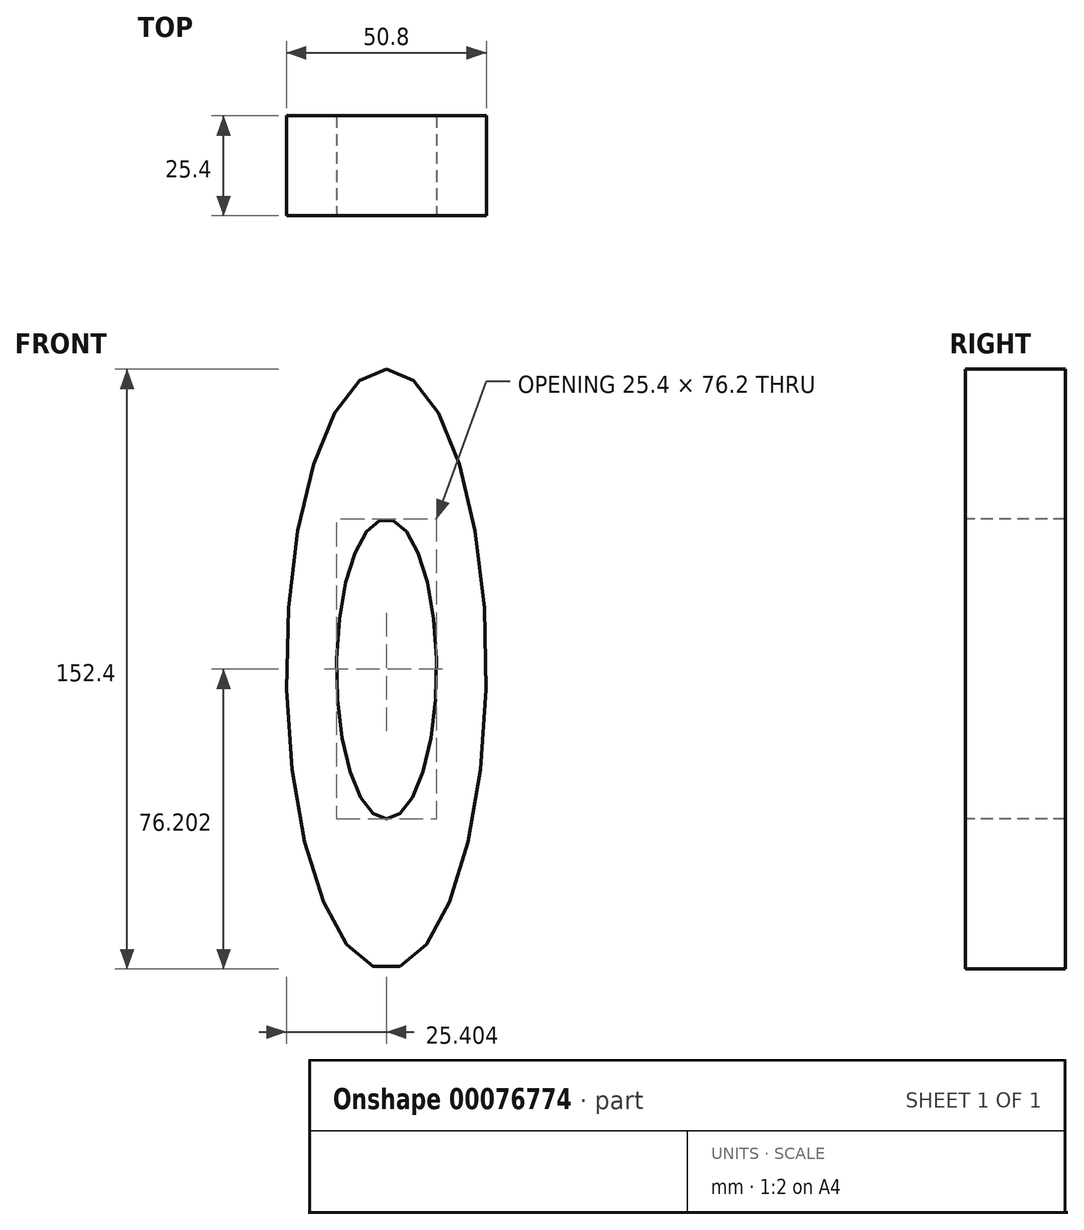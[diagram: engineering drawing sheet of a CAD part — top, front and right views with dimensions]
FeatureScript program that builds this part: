
annotation { "Feature Type Name" : "Feature", "Feature Type Description" : "" }
export const myFeature = defineFeature(function(context is Context, id is Id, definition is map)
    precondition{}
    {
        {
            var Q0;
            Q0=qCreatedBy(makeId("Front.planeOp"),FACE);
            var sketch = newSketch(context, id + "F0", { "sketchPlane" : qUnion([Q0])});
            skEllipse(sketch, "E0", {"center": v(-19.88, 8.25) * mm, "majorRadius": 25.4 * mm, "minorRadius": 76.2 * mm, "majorAxis": v(1, 0)});
            skPoint(sketch, "E1.orphan", {"position": v(-45.28, 8.25) * mm});
            skPoint(sketch, "E2.end.orphan", {"position": v(5.52, 8.25) * mm});
            skSolve(sketch);
        }
        {
            var Q0;
            Q0=makeQuery(id+"F0.imprint","IMPRINT",FACE,{"disambiguationData":[TD([[makeQuery(id+"F0.imprint","IMPRINT",EDGE,{"derivedFrom":sQuery(id+"F0.wireOp",EDGE,"E0")}),1.0]])]});
            extrude(context, id + "F1", {"entities" : qUnion([Q0]), "depth" : 25.4 * mm});
        }
        {
            var Q0;
            Q0=makeQuery(id+"F1.opExtrude","CAP_FACE",FACE,{"disambiguationData":[OSD([sQuery(id+"F0.wireOp",EDGE,"E0")])],"isStart":false});
            var sketch = newSketch(context, id + "F2", { "sketchPlane" : qUnion([Q0])});
            skEllipse(sketch, "E3", {"center": v(-19.88, 8.25) * mm, "majorRadius": 38.1 * mm, "minorRadius": 12.7 * mm, "majorAxis": v(0, -1)});
            skSolve(sketch);
        }
        {
            var Q0;
            Q0=makeQuery(id+"F2.imprint","IMPRINT",FACE,{"disambiguationData":[TD([[makeQuery(id+"F2.imprint","IMPRINT",EDGE,{"derivedFrom":sQuery(id+"F2.wireOp",EDGE,"E3")}),1.0]])]});
            extrude(context, id + "F3", {"entities" : qUnion([Q0]), "operationType" : NewBodyOperationType.REMOVE, "oppositeDirection" : true, "depth" : 25.4 * mm});
        }
    });
